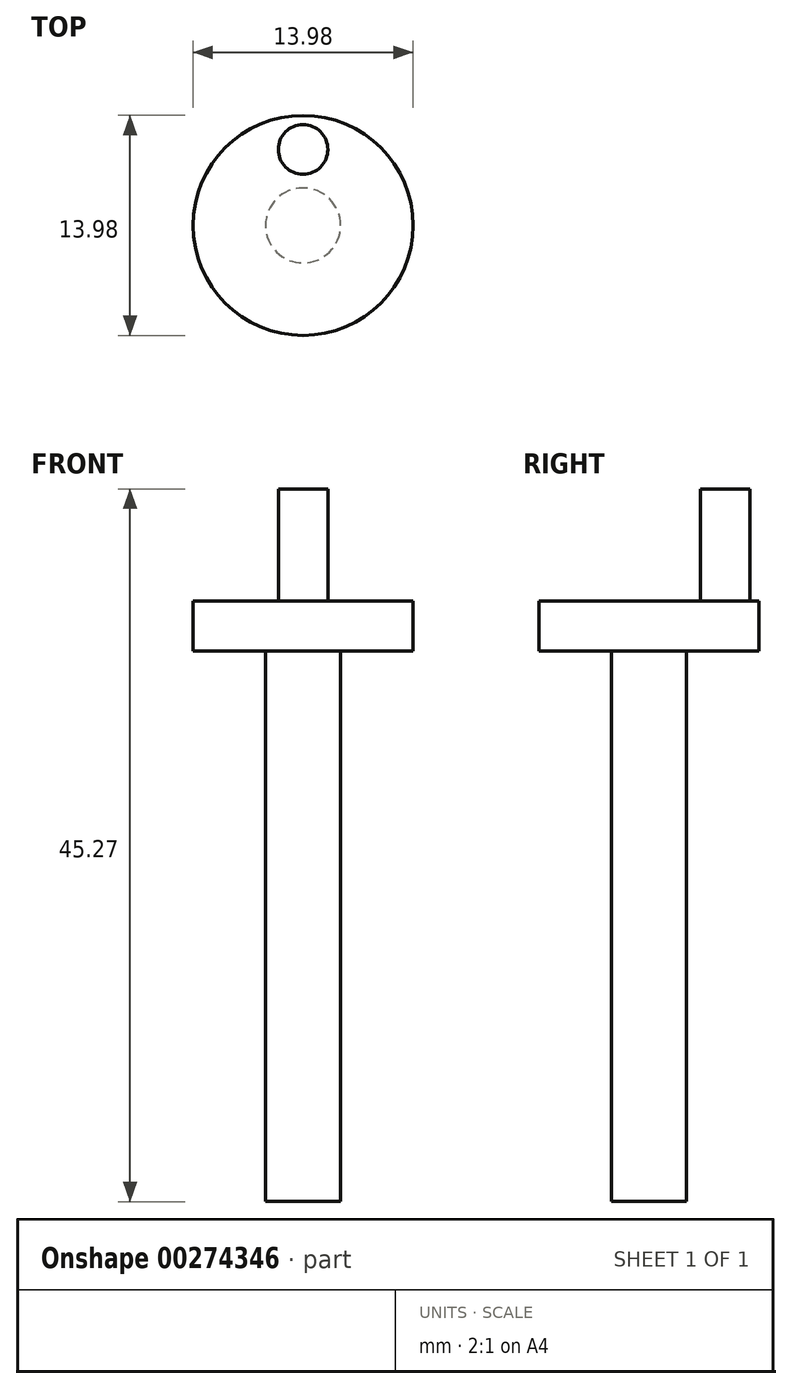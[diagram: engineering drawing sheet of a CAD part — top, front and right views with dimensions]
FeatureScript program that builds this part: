
annotation { "Feature Type Name" : "Feature", "Feature Type Description" : "" }
export const myFeature = defineFeature(function(context is Context, id is Id, definition is map)
    precondition{}
    {
        {
            var Q0;
            Q0=qCreatedBy(makeId("Top.planeOp"),FACE);
            var sketch = newSketch(context, id + "F0", { "sketchPlane" : qUnion([Q0])});
            skCircle(sketch, "E0", {"center": v(0, 0) * mm, "radius": 6.99 * mm});
            skCircle(sketch, "E1", {"center": v(0, 4.83) * mm, "radius": 1.57 * mm, "construction": true});
            skCircle(sketch, "E2", {"center": v(0, 0) * mm, "radius": 2.38 * mm, "construction": true});
            skSolve(sketch);
        }
        {
            var Q0;
            Q0=makeQuery(id+"F0.imprint","IMPRINT",FACE,{"disambiguationData":[TD([[makeQuery(id+"F0.imprint","IMPRINT",EDGE,{"derivedFrom":sQuery(id+"F0.wireOp",EDGE,"E0")}),1.0]])]});
            extrude(context, id + "F1", {"entities" : qUnion([Q0]), "depth" : 3.17 * mm});
        }
        {
            var Q0;
            Q0=makeQuery(id+"F0.imprint","IMPRINT",FACE,{"disambiguationData":[TD([[makeQuery(id+"F0.imprint","IMPRINT",EDGE,{"derivedFrom":sQuery(id+"F0.wireOp",EDGE,"E0")}),1.0]])]});
            var sketch = newSketch(context, id + "F2", { "sketchPlane" : qUnion([Q0])});
            skCircle(sketch, "E3.0", {"center": v(0, 0) * mm, "radius": 2.38 * mm});
            skSolve(sketch);
        }
        {
            var Q0;
            Q0 = qSketchRegion(id + "F2", true);
            extrude(context, id + "F3", {"entities" : qUnion([Q0]), "operationType" : NewBodyOperationType.ADD, "oppositeDirection" : true, "depth" : 34.98 * mm});
        }
        {
            var Q0;
            Q0=makeQuery(id+"F1.opExtrude","CAP_FACE",FACE,{"disambiguationData":[OSD([sQuery(id+"F0.wireOp",EDGE,"E0")])],"isStart":false});
            var sketch = newSketch(context, id + "F4", { "sketchPlane" : qUnion([Q0])});
            skCircle(sketch, "E4.0", {"center": v(0, 4.83) * mm, "radius": 1.57 * mm});
            skSolve(sketch);
        }
        {
            var Q0;
            Q0 = qSketchRegion(id + "F4", true);
            extrude(context, id + "F5", {"entities" : qUnion([Q0]), "operationType" : NewBodyOperationType.ADD, "depth" : 7.11 * mm});
        }
    });
